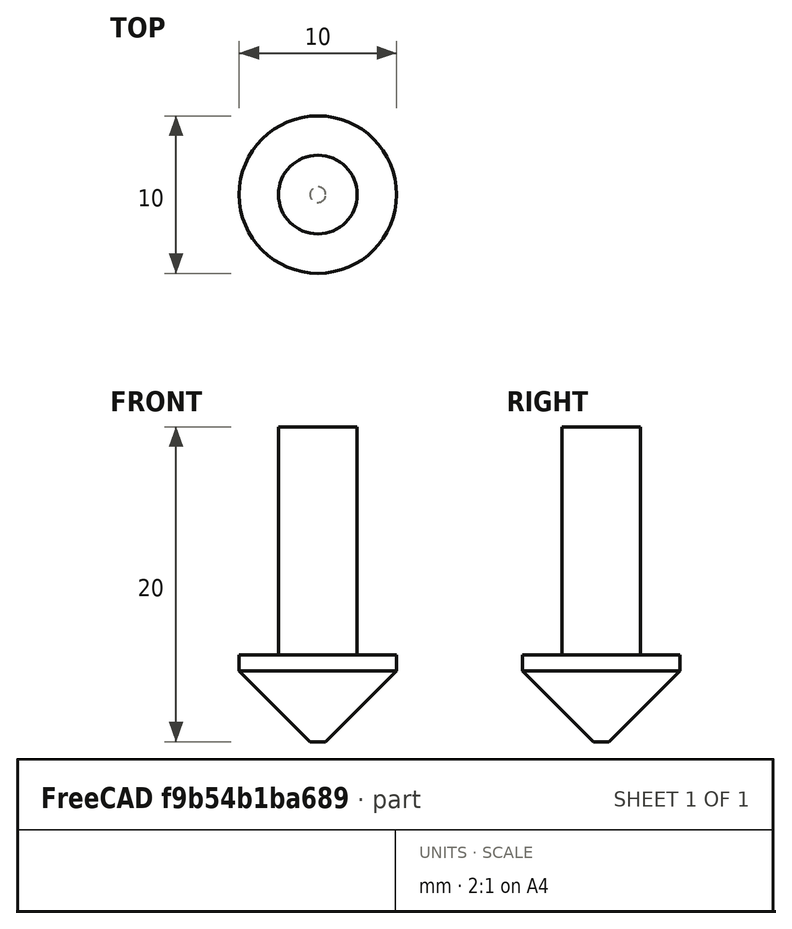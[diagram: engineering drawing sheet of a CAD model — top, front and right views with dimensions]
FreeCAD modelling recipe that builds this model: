
FCSTD DOCUMENT  (FreeCAD 0.19R24049 (Git))
Label: v-bit
License: All rights reserved
LicenseURL: http://en.wikipedia.org/wiki/All_rights_reserved
objects: Sketcher::SketchObject×1, PartDesign::Revolution×1, App::FeaturePython×1, PartDesign::Body×1
note: 4 computed .brp shape members not serialized (recipe doc carries the construction recipe); baked Part::Feature solids carry a one-line shape summary decoded from their .brp

FEATURE [Sketcher::SketchObject] Sketch
  FullyConstrained = true
  MapMode = 5
  Placement = pos=(0,0,0) rot=(1,0,0;1.5708rad)
  Support = -> [XZ_Plane]
  expr: Constraints[28] = <<Attributes>>.TipDiameter
  expr: Constraints[17] = <<Attributes>>.Diameter
  expr: Constraints[22] = <<Attributes>>.ShankDiameter
  expr: Constraints[19] = <<Attributes>>.Length
  expr: Constraints[18] = <<Attributes>>.CuttingEdgeAngle
  expr: Constraints[26] = <<Attributes>>.CuttingEdgeHeight
  sketch-geometry (12):
    g0: LineSegment StartX=0 StartY=20 StartZ=0 EndX=0 EndY=0 EndZ=0
    g1: LineSegment StartX=0 StartY=0 StartZ=0 EndX=0.5 EndY=0 EndZ=0
    g2: LineSegment StartX=0.5 StartY=0 StartZ=0 EndX=5 EndY=4.5 EndZ=0
    g3: LineSegment StartX=5 StartY=5.5 StartZ=0 EndX=2.5 EndY=5.49 EndZ=0
    g4: LineSegment StartX=2.5 StartY=5.49 StartZ=0 EndX=2.5 EndY=20 EndZ=0
    g5: LineSegment StartX=2.5 StartY=20 StartZ=0 EndX=0 EndY=20 EndZ=0
    g6: LineSegment StartX=-5 StartY=4.5 StartZ=0 EndX=5 EndY=4.5 EndZ=0
    g7: LineSegment StartX=5 StartY=4.5 StartZ=0 EndX=0.5 EndY=0 EndZ=0
    g8: LineSegment StartX=0.5 StartY=0 StartZ=0 EndX=-0.5 EndY=0 EndZ=0
    g9: LineSegment StartX=-0.5 StartY=0 StartZ=0 EndX=-5 EndY=4.5 EndZ=0
    g10: LineSegment StartX=2.5 StartY=20 StartZ=0 EndX=-2.5 EndY=20 EndZ=0
    g11: LineSegment StartX=5 StartY=4.5 StartZ=0 EndX=5 EndY=5.5 EndZ=0
  constraints (30):
    c: Vertical(g0)
    c: Coincident(g0,g1)
    c: Horizontal(g1)
    c: Coincident(g1,g2)
    c: Coincident(g3,g4)
    c: Vertical(g4)
    c: Coincident(g4,g5)
    c: Horizontal(g5)
    c: Coincident(g5,g0)
    c: Coincident(g6,g7)
    c: Coincident(g7,g8)
    c: Coincident(g8,g9)
    c: Coincident(g9,g6)
    c: Symmetric(g8,g7,g0)
    c: Coincident(g1,g7)
    c: Coincident(g2,g6)
    c: Symmetric(g2,g6,g0)
    c: DistanceX(g6,g6) = 10
    c: Angle(g2,g9) = 1.5708
    c: DistanceY(g0,g0) = 20
    c: Coincident(g10,g4)
    c: Symmetric(g10,g4,g-2)
    c: DistanceX(g10,g10) = 5
    c: Vertical(g11)
    c: Coincident(g3,g11)
    c: Coincident(g11,g2)
    c: DistanceY(g11,g11) = 1
    c: Coincident(g-1,g0)
    c: DistanceX(g8,g8) = 1
    c: DistanceY(g3,g3) = 0.01
FEATURE [PartDesign::Revolution] Revolution
  AllowMultiFace = false
  Angle = 360
  Axis = (0,-2e-16,1)
  Base = (0,0,0)
  Placement = pos=(0,0,0) rot=(1,0,0;1.5708rad)
  Profile = -> Sketch
  ReferenceAxis = -> Sketch [V_Axis]
  Reversed = true
FEATURE [App::FeaturePython] PropertyBag  label="Attributes"  # WARN: FeaturePython — macro-defined, semantics opaque (R4)
  Chipload = 0
  CustomPropertyGroups = Attributes | Shape
  CuttingEdgeAngle = 90
  CuttingEdgeHeight = 1
  Diameter = 10
  Flutes = 0
  Length = 20
  Material = 0
  ShankDiameter = 5
  TipDiameter = 1
FEATURE [PartDesign::Body] Body  label="V-Bit"
  Group = -> [Sketch,Revolution,PropertyBag]
  Origin = -> Origin
  Tip = -> Revolution
